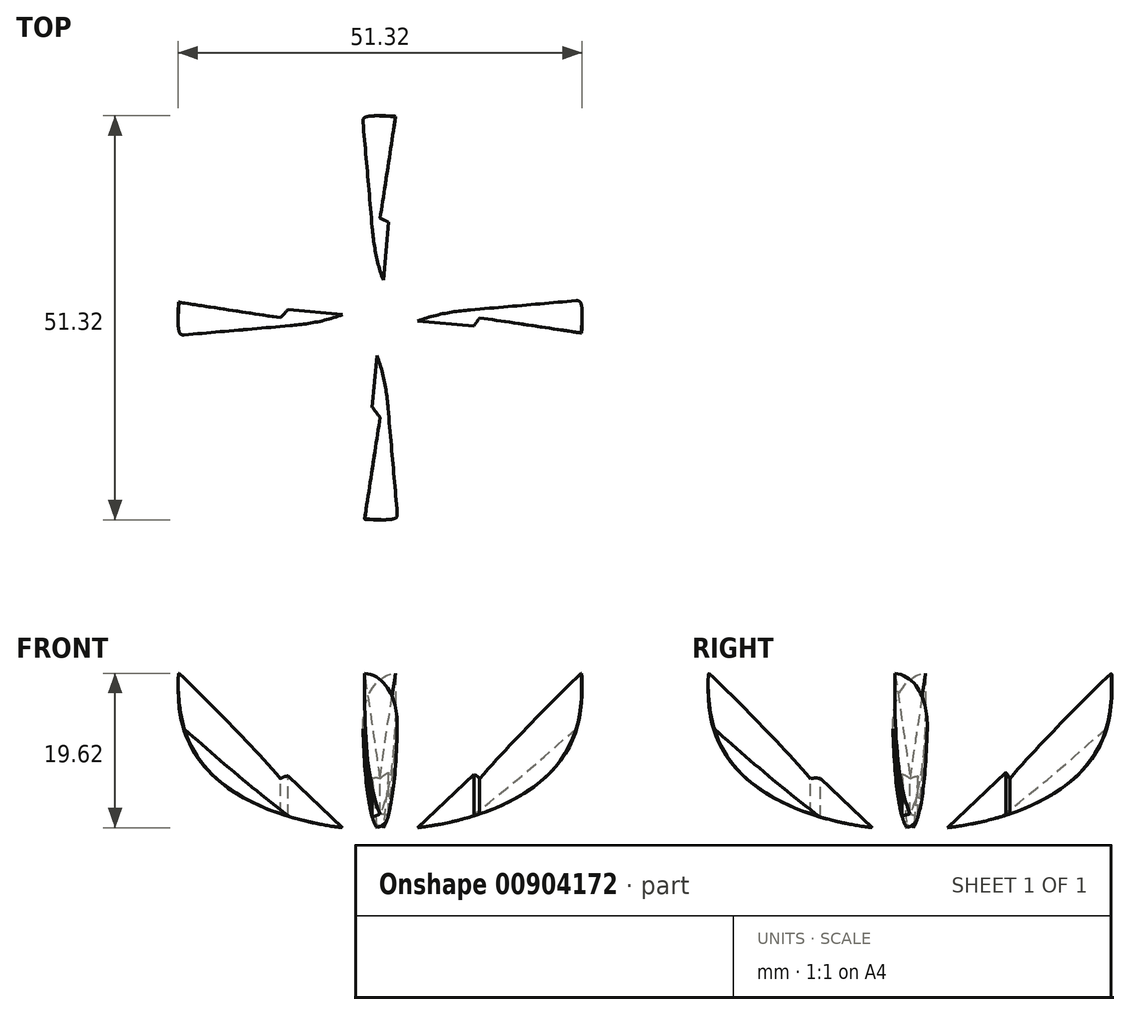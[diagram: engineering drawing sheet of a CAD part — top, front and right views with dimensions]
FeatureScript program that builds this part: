
annotation { "Feature Type Name" : "Feature", "Feature Type Description" : "" }
export const myFeature = defineFeature(function(context is Context, id is Id, definition is map)
    precondition{}
    {
        {
            var Q0;
            Q0=qCreatedBy(makeId("Front.planeOp"),FACE);
            var sketch = newSketch(context, id + "F0", { "sketchPlane" : qUnion([Q0])});
            skLineSegment(sketch, "E0", {"start": v(-28.58, 0) * mm, "end": v(28.58, 0) * mm, "construction": true});
            skLineSegment(sketch, "E1", {"start": v(0, 0) * mm, "end": v(0, -50.8) * mm, "construction": true});
            skLineSegment(sketch, "E2", {"start": v(-12.7, -50.8) * mm, "end": v(12.7, -50.8) * mm, "construction": true});
            skLineSegment(sketch, "E3", {"start": v(0, 0) * mm, "end": v(0, -12.7) * mm, "construction": true});
            skLineSegment(sketch, "E4", {"start": v(-23.5, -12.7) * mm, "end": v(23.5, -12.7) * mm, "construction": true});
            skLineSegment(sketch, "E5", {"start": v(0, -50.8) * mm, "end": v(0, -38.1) * mm, "construction": true});
            skLineSegment(sketch, "E6", {"start": v(-25.4, -38.1) * mm, "end": v(25.4, -38.1) * mm, "construction": true});
            skLineSegment(sketch, "E7", {"start": v(0, -52.8) * mm, "end": v(0, -57.57) * mm, "construction": true});
            skLineSegment(sketch, "E8", {"start": v(-19.77, -52.8) * mm, "end": v(-17.38, -48.69) * mm, "construction": true});
            skLineSegment(sketch, "E9", {"start": v(-28.25, -13.02) * mm, "end": v(-23.5, -12.7) * mm, "construction": true});
            skLineSegment(sketch, "E10", {"start": v(23.5, -12.7) * mm, "end": v(28.25, -12.93) * mm, "construction": true});
            skLineSegment(sketch, "E11", {"start": v(-25.4, -38.1) * mm, "end": v(-29.76, -40.01) * mm, "construction": true});
            skLineSegment(sketch, "E12", {"start": v(25.4, -38.1) * mm, "end": v(30.07, -39.03) * mm, "construction": true});
            skLineSegment(sketch, "E13", {"start": v(16.77, -49.02) * mm, "end": v(19.05, -53.2) * mm, "construction": true});
            skLineSegment(sketch, "E14", {"start": v(-28.58, 0) * mm, "end": v(-34.9, -3.29) * mm, "construction": true});
            skLineSegment(sketch, "E15", {"start": v(28.58, 0) * mm, "end": v(34.58, -3.85) * mm, "construction": true});
            skLineSegment(sketch, "E16", {"start": v(0, -52.8) * mm, "end": v(0, -57.57) * mm});
            skFitSpline(sketch, "E17", {"points": [v(0, -57.57) * mm, v(19.05, -53.2) * mm, v(30.07, -39.03) * mm, v(28.25, -12.93) * mm, v(34.58, -3.85) * mm, v(28.57, 0) * mm, v(23.5, -12.7) * mm, v(25.4, -38.1) * mm, v(16.77, -49.02) * mm, v(0, -52.8) * mm, v(-17.38, -48.69) * mm, v(-25.4, -38.1) * mm, v(-23.5, -12.7) * mm, v(-28.57, 0) * mm, v(-34.9, -3.29) * mm, v(-28.25, -13.02) * mm, v(-29.76, -40.01) * mm, v(-19.77, -52.8) * mm, v(0, -57.57) * mm]});
            skLineSegment(sketch, "E18", {"start": v(-25.62, -32.87) * mm, "end": v(-29.42, -32.87) * mm, "construction": true});
            skFitSpline(sketch, "E19", {"points": [v(-25.62, -32.87) * mm, v(-4.79, -52.5) * mm], "startDerivative": vector(17.85, -29.52) * mm, "endDerivative": vector(38.14, -17.66) * mm});
            skLineSegment(sketch, "E20", {"start": v(-25.62, -32.87) * mm, "end": v(-4.79, -52.5) * mm});
            skSolve(sketch);
        }
        {
            var Q0;
            {var subQ1=sQuery(id+"F0.wireOp",EDGE,"E19");Q0=makeQuery(id+"F0.imprint","IMPRINT",FACE,{"disambiguationData":[TD([[makeQuery(id+"F0.imprint","IMPRINT",EDGE,{"derivedFrom":subQ1}),-1.0]])]});}
            var Q1;
            Q1=makeQuery(id+"F0.imprint","IMPRINT",FACE,{"disambiguationData":[TD([[makeQuery(id+"F0.imprint","IMPRINT",EDGE,{"derivedFrom":sQuery(id+"F0.wireOp",EDGE,"E19")}),1.0]])]});
            var Q2;
            Q2=sQuery(id+"F0.wireOp",EDGE,"E1");
            revolve(context, id + "F1", {"surfaceOperationType" : NewSurfaceOperationType.NEW, "entities" : qUnion([Q0, Q1]), "axis" : qUnion([Q2]), "revolveType" : RevolveType.TWO_DIRECTIONS, "angle" : 5 * degree, "angleBack" : 355 * degree});
        }
        {
            var Q0;
            {var subQ1=sQuery(id+"F0.wireOp",EDGE,"E19");Q0=makeQuery(id+"F0.imprint","IMPRINT",FACE,{"disambiguationData":[TD([[makeQuery(id+"F0.imprint","IMPRINT",EDGE,{"derivedFrom":subQ1}),-1.0]])]});}
            var Q1;
            Q1=makeQuery(id+"F0.imprint","IMPRINT",FACE,{"disambiguationData":[TD([[makeQuery(id+"F0.imprint","IMPRINT",EDGE,{"derivedFrom":sQuery(id+"F0.wireOp",EDGE,"E19")}),1.0]])]});
            var Q2;
            Q2=sQuery(id+"F0.wireOp",EDGE,"E5");
            revolve(context, id + "F2", {"surfaceOperationType" : NewSurfaceOperationType.NEW, "entities" : qUnion([Q0, Q1]), "axis" : qUnion([Q2]), "revolveType" : RevolveType.TWO_DIRECTIONS, "angle" : 185 * degree, "angleBack" : 175 * degree});
        }
        {
            var Q0;
            {var subQ1=sQuery(id+"F0.wireOp",EDGE,"E19");Q0=makeQuery(id+"F0.imprint","IMPRINT",FACE,{"disambiguationData":[TD([[makeQuery(id+"F0.imprint","IMPRINT",EDGE,{"derivedFrom":subQ1}),-1.0]])]});}
            var Q1;
            Q1=makeQuery(id+"F0.imprint","IMPRINT",FACE,{"disambiguationData":[TD([[makeQuery(id+"F0.imprint","IMPRINT",EDGE,{"derivedFrom":sQuery(id+"F0.wireOp",EDGE,"E19")}),1.0]])]});
            var Q2;
            Q2=sQuery(id+"F0.wireOp",EDGE,"E5");
            revolve(context, id + "F3", {"surfaceOperationType" : NewSurfaceOperationType.NEW, "entities" : qUnion([Q0, Q1]), "axis" : qUnion([Q2]), "revolveType" : RevolveType.TWO_DIRECTIONS, "angle" : 275 * degree, "angleBack" : 265 * degree});
        }
        {
            var Q0;
            {var subQ1=sQuery(id+"F0.wireOp",EDGE,"E19");Q0=makeQuery(id+"F0.imprint","IMPRINT",FACE,{"disambiguationData":[TD([[makeQuery(id+"F0.imprint","IMPRINT",EDGE,{"derivedFrom":subQ1}),-1.0]])]});}
            var Q1;
            Q1=makeQuery(id+"F0.imprint","IMPRINT",FACE,{"disambiguationData":[TD([[makeQuery(id+"F0.imprint","IMPRINT",EDGE,{"derivedFrom":sQuery(id+"F0.wireOp",EDGE,"E19")}),1.0]])]});
            var Q2;
            Q2=sQuery(id+"F0.wireOp",EDGE,"E5");
            revolve(context, id + "F4", {"surfaceOperationType" : NewSurfaceOperationType.NEW, "entities" : qUnion([Q0, Q1]), "axis" : qUnion([Q2]), "revolveType" : RevolveType.TWO_DIRECTIONS, "angle" : 95 * degree, "angleBack" : 85 * degree});
        }
        {
            var Q0;
            Q0=qCreatedBy(makeId("Top.planeOp"),FACE);
            var sketch = newSketch(context, id + "F5", { "sketchPlane" : qUnion([Q0])});
            skCircle(sketch, "E21", {"center": v(0, 0) * mm, "radius": 29.84 * mm, "construction": true});
            skLineSegment(sketch, "E22", {"start": v(0, 0) * mm, "end": v(-29.72, -2.6) * mm, "construction": true});
            skLineSegment(sketch, "E23", {"start": v(0, 0) * mm, "end": v(-29.72, 2.61) * mm, "construction": true});
            skLineSegment(sketch, "E24", {"start": v(0, 0) * mm, "end": v(-12.65, -1.1) * mm, "construction": true});
            skLineSegment(sketch, "E25", {"start": v(0, 0) * mm, "end": v(-12.65, 1.11) * mm, "construction": true});
            skLineSegment(sketch, "E26", {"start": v(-12.65, 1.11) * mm, "end": v(-12.65, -1.1) * mm, "construction": true});
            skLineSegment(sketch, "E27", {"start": v(-29.72, -2.6) * mm, "end": v(-12.65, 0) * mm});
            skPoint(sketch, "E27.endSnap0", {"position": v(-12.65, 0) * mm});
            skLineSegment(sketch, "E28", {"start": v(-12.65, 0) * mm, "end": v(-12.01, -1.05) * mm});
            skLineSegment(sketch, "E29", {"start": v(-12.01, -1.05) * mm, "end": v(-29.44, -4.84) * mm});
            skLineSegment(sketch, "E30", {"start": v(-29.44, -4.84) * mm, "end": v(-29.72, -2.6) * mm});
            skLineSegment(sketch, "E31", {"start": v(-29.72, 2.61) * mm, "end": v(-12.65, 0) * mm});
            skLineSegment(sketch, "E32", {"start": v(-12.65, 0) * mm, "end": v(-11.7, 1.03) * mm});
            skLineSegment(sketch, "E33", {"start": v(-11.7, 1.03) * mm, "end": v(-29.44, 4.84) * mm});
            skLineSegment(sketch, "E34", {"start": v(-29.44, 4.84) * mm, "end": v(-29.72, 2.61) * mm});
            skLineSegment(sketch, "E35", {"start": v(0, 29.84) * mm, "end": v(0, 0) * mm, "construction": true});
            skLineSegment(sketch, "E36", {"start": v(0, 29.84) * mm, "end": v(2.62, 29.84) * mm, "construction": true});
            skLineSegment(sketch, "E37", {"start": v(2.62, 29.84) * mm, "end": v(0, 0) * mm, "construction": true});
            skLineSegment(sketch, "E38", {"start": v(0, 29.84) * mm, "end": v(-2.62, 29.84) * mm, "construction": true});
            skLineSegment(sketch, "E39", {"start": v(-2.62, 29.84) * mm, "end": v(0, -0.83) * mm, "construction": true});
            skLineSegment(sketch, "E40", {"start": v(0, 0) * mm, "end": v(1.1, 12.65) * mm, "construction": true});
            skLineSegment(sketch, "E41", {"start": v(0, 0) * mm, "end": v(-1.15, 12.65) * mm, "construction": true});
            skLineSegment(sketch, "E42", {"start": v(-1.15, 12.65) * mm, "end": v(1.1, 12.65) * mm, "construction": true});
            skLineSegment(sketch, "E43", {"start": v(-2.62, 29.84) * mm, "end": v(0, 12.65) * mm});
            skLineSegment(sketch, "E44", {"start": v(0, 12.65) * mm, "end": v(2.62, 29.84) * mm});
            skLineSegment(sketch, "E45", {"start": v(0, 12.65) * mm, "end": v(-1.1, 12.02) * mm});
            skLineSegment(sketch, "E46", {"start": v(-1.1, 12.02) * mm, "end": v(-5.18, 29.38) * mm});
            skLineSegment(sketch, "E47", {"start": v(-5.18, 29.38) * mm, "end": v(-2.62, 29.84) * mm});
            skLineSegment(sketch, "E48", {"start": v(0, 12.65) * mm, "end": v(1.07, 12.16) * mm});
            skLineSegment(sketch, "E49", {"start": v(1.07, 12.16) * mm, "end": v(5.06, 29.4) * mm});
            skLineSegment(sketch, "E50", {"start": v(5.06, 29.4) * mm, "end": v(2.62, 29.84) * mm});
            skLineSegment(sketch, "E51", {"start": v(0, 0) * mm, "end": v(29.84, 0) * mm, "construction": true});
            skLineSegment(sketch, "E52", {"start": v(29.84, 0) * mm, "end": v(29.84, 2.62) * mm, "construction": true});
            skLineSegment(sketch, "E53", {"start": v(29.84, 2.62) * mm, "end": v(0, 0) * mm, "construction": true});
            skLineSegment(sketch, "E54", {"start": v(29.84, 0) * mm, "end": v(30.07, -2.6) * mm, "construction": true});
            skLineSegment(sketch, "E55", {"start": v(30.07, -2.6) * mm, "end": v(0, 0) * mm, "construction": true});
            skLineSegment(sketch, "E56", {"start": v(0, 0) * mm, "end": v(12.65, -1.1) * mm, "construction": true});
            skLineSegment(sketch, "E57", {"start": v(0, 0) * mm, "end": v(12.65, 1.1) * mm, "construction": true});
            skLineSegment(sketch, "E58", {"start": v(12.65, 1.1) * mm, "end": v(12.65, -1.1) * mm});
            skLineSegment(sketch, "E59", {"start": v(29.84, 2.62) * mm, "end": v(12.65, 0) * mm});
            skLineSegment(sketch, "E60", {"start": v(12.65, 0) * mm, "end": v(11.26, 0.99) * mm});
            skLineSegment(sketch, "E61", {"start": v(11.26, 0.99) * mm, "end": v(29.35, 5.38) * mm});
            skLineSegment(sketch, "E62", {"start": v(29.35, 5.38) * mm, "end": v(29.84, 2.62) * mm});
            skLineSegment(sketch, "E63", {"start": v(30.07, -2.6) * mm, "end": v(12.65, 0) * mm});
            skLineSegment(sketch, "E64", {"start": v(12.65, 0) * mm, "end": v(11.87, -1.1) * mm});
            skLineSegment(sketch, "E65", {"start": v(11.87, -1.1) * mm, "end": v(29.15, -6.35) * mm});
            skLineSegment(sketch, "E66", {"start": v(29.15, -6.35) * mm, "end": v(30.07, -2.6) * mm});
            skLineSegment(sketch, "E67", {"start": v(0, 0) * mm, "end": v(0, -29.84) * mm, "construction": true});
            skLineSegment(sketch, "E68", {"start": v(0, -29.84) * mm, "end": v(2.62, -29.84) * mm, "construction": true});
            skLineSegment(sketch, "E69", {"start": v(2.62, -29.84) * mm, "end": v(0, 0) * mm, "construction": true});
            skLineSegment(sketch, "E70", {"start": v(0, -29.84) * mm, "end": v(-2.62, -29.84) * mm, "construction": true});
            skLineSegment(sketch, "E71", {"start": v(-2.62, -29.84) * mm, "end": v(0, 0) * mm, "construction": true});
            skLineSegment(sketch, "E72", {"start": v(0, 0) * mm, "end": v(1.1, -12.65) * mm, "construction": true});
            skLineSegment(sketch, "E73", {"start": v(0, 0) * mm, "end": v(-1.1, -12.65) * mm, "construction": true});
            skLineSegment(sketch, "E74", {"start": v(-1.1, -12.65) * mm, "end": v(1.1, -12.65) * mm, "construction": true});
            skLineSegment(sketch, "E75", {"start": v(0, -12.65) * mm, "end": v(-2.62, -29.84) * mm});
            skLineSegment(sketch, "E76", {"start": v(0, -12.65) * mm, "end": v(2.62, -29.84) * mm});
            skLineSegment(sketch, "E77", {"start": v(0, -12.65) * mm, "end": v(-1, -11.37) * mm});
            skLineSegment(sketch, "E78", {"start": v(-1, -11.37) * mm, "end": v(-5.8, -29.27) * mm});
            skLineSegment(sketch, "E79", {"start": v(-5.8, -29.27) * mm, "end": v(-2.62, -29.84) * mm});
            skLineSegment(sketch, "E80", {"start": v(2.62, -29.84) * mm, "end": v(6.49, -29.12) * mm});
            skLineSegment(sketch, "E81", {"start": v(6.49, -29.12) * mm, "end": v(1.02, -11.66) * mm});
            skLineSegment(sketch, "E82", {"start": v(1.02, -11.66) * mm, "end": v(0, -12.65) * mm});
            skSolve(sketch);
        }
        {
            var Q0;
            Q0=makeQuery(id+"F1.opRevolve","CAP_EDGE",EDGE,{"disambiguationData":[OSD([sQuery(id+"F0.wireOp",EDGE,"E20")])],"isStart":true});
            var Q1;
            Q1=makeQuery(id+"F4.opRevolve","CAP_EDGE",EDGE,{"disambiguationData":[OSD([sQuery(id+"F0.wireOp",EDGE,"E20")])],"isStart":false});
            var Q2;
            Q2=makeQuery(id+"F3.opRevolve","CAP_EDGE",EDGE,{"disambiguationData":[OSD([sQuery(id+"F0.wireOp",EDGE,"E20")])],"isStart":false});
            var Q3;
            Q3=makeQuery(id+"F2.opRevolve","CAP_EDGE",EDGE,{"disambiguationData":[OSD([sQuery(id+"F0.wireOp",EDGE,"E20")])],"isStart":false});
            fillet(context, id + "F6", {"entities" : qUnion([Q0, Q1, Q2, Q3]), "tangentPropagation" : true, "radius" : 5.08 * mm, "defaultsChanged" : false, "vertexSettings" : [], "allowEdgeOverflow" : false});
        }
        {
            var Q0;
            Q0=makeQuery(id+"F5.imprint","IMPRINT",FACE,{"disambiguationData":[TD([[makeQuery(id+"F5.imprint","IMPRINT",EDGE,{"derivedFrom":sQuery(id+"F5.wireOp",EDGE,"E75")}),-1.0]])]});
            var Q1;
            Q1=makeQuery(id+"F5.imprint","IMPRINT",FACE,{"disambiguationData":[TD([[makeQuery(id+"F5.imprint","IMPRINT",EDGE,{"derivedFrom":sQuery(id+"F5.wireOp",EDGE,"E31")}),1.0]])]});
            var Q2;
            Q2=makeQuery(id+"F5.imprint","IMPRINT",FACE,{"disambiguationData":[TD([[makeQuery(id+"F5.imprint","IMPRINT",EDGE,{"derivedFrom":sQuery(id+"F5.wireOp",EDGE,"E44")}),-1.0]])]});
            var Q3;
            Q3=makeQuery(id+"F5.imprint","IMPRINT",FACE,{"disambiguationData":[TD([[makeQuery(id+"F5.imprint","IMPRINT",EDGE,{"derivedFrom":sQuery(id+"F5.wireOp",EDGE,"E63")}),1.0]])]});
            extrude(context, id + "F7", {"entities" : qUnion([Q0, Q1, Q2, Q3]), "operationType" : NewBodyOperationType.REMOVE, "endBound" : BoundingType.THROUGH_ALL, "oppositeDirection" : true, "depth" : 25.4 * mm, "offsetDistance" : 25.4 * mm});
        }
    });
